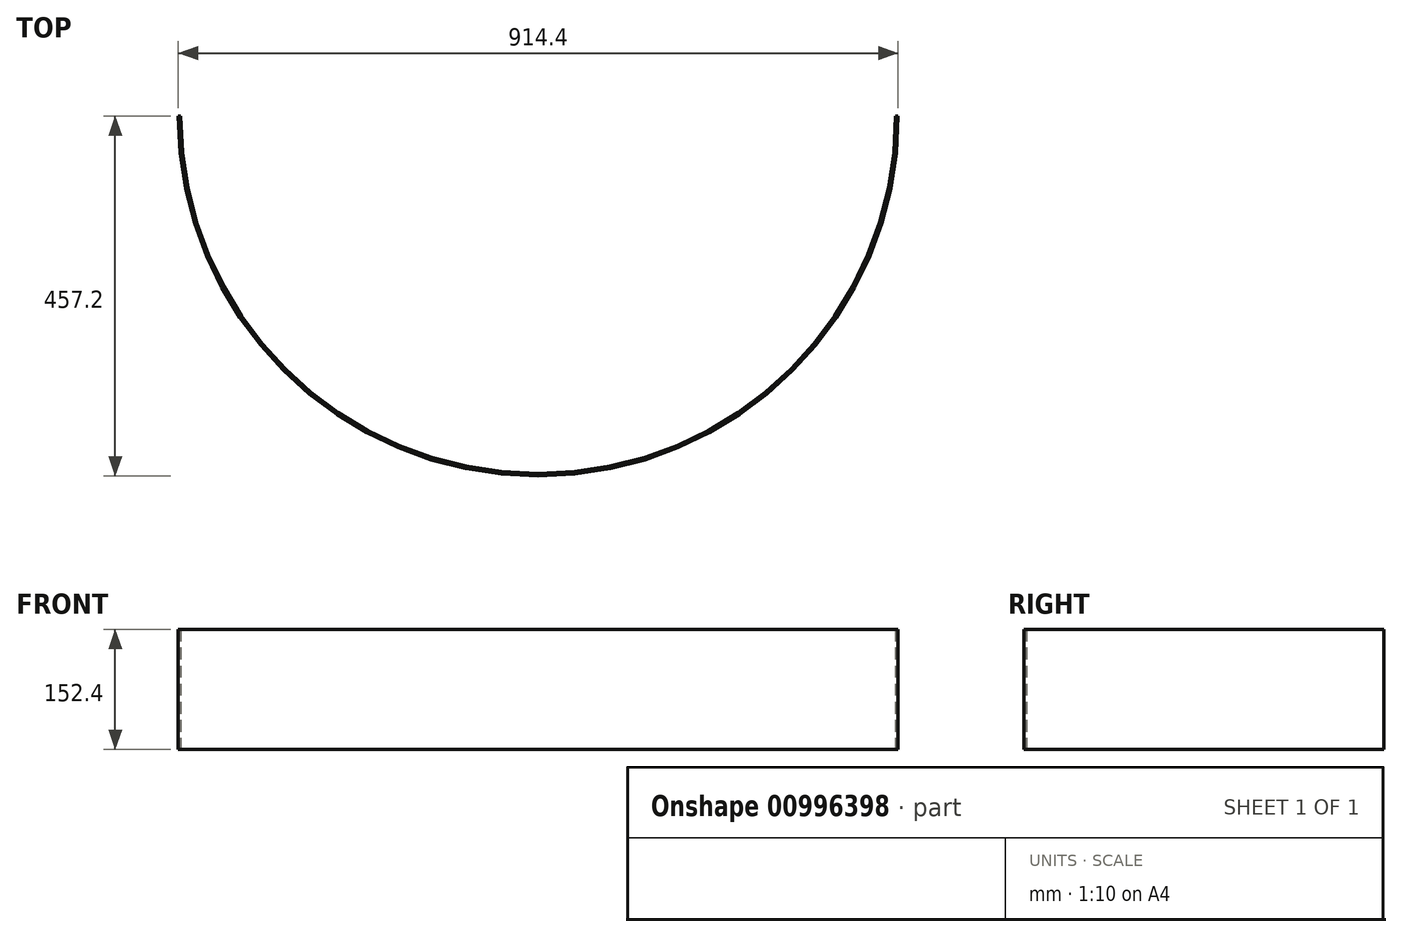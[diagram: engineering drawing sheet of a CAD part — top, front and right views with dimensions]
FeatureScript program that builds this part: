
annotation { "Feature Type Name" : "Feature", "Feature Type Description" : "" }
export const myFeature = defineFeature(function(context is Context, id is Id, definition is map)
    precondition{}
    {
        {
            var Q0;
            Q0=qCreatedBy(makeId("Top.planeOp"),FACE);
            var sketch = newSketch(context, id + "F0", { "sketchPlane" : qUnion([Q0])});
            skArc(sketch, "E0", {"start": v(0, 0) * mm, "mid": v(457.2, -457.2) * mm, "end": v(914.4, 0) * mm});
            skLineSegment(sketch, "E1", {"start": v(914.4, 0) * mm, "end": v(0, 0) * mm});
            skSolve(sketch);
        }
        {
            var Q0;
            Q0 = qSketchRegion(id + "F0", true);
            extrude(context, id + "F1", {"entities" : qUnion([Q0]), "depth" : 152.4 * mm, "offsetDistance" : 25.4 * mm});
        }
        {
            var Q0;
            Q0=makeQuery(id+"F1.opExtrude","CAP_FACE",FACE,{"disambiguationData":[OSD([sQuery(id+"F0.wireOp",EDGE,"E0"),sQuery(id+"F0.wireOp",EDGE,"E1")])],"isStart":false});
            var Q1;
            Q1=makeQuery(id+"F1.opExtrude","SWEPT_FACE",FACE,{"disambiguationData":[OSD([sQuery(id+"F0.wireOp",EDGE,"E1")])]});
            var Q2;
            Q2=makeQuery(id+"F1.opExtrude","CAP_FACE",FACE,{"disambiguationData":[OSD([sQuery(id+"F0.wireOp",EDGE,"E0"),sQuery(id+"F0.wireOp",EDGE,"E1")])],"isStart":true});
            shell(context, id + "F2", {"entities" : qUnion([Q0, Q1, Q2]), "thickness" : 3.17 * mm});
        }
    });
